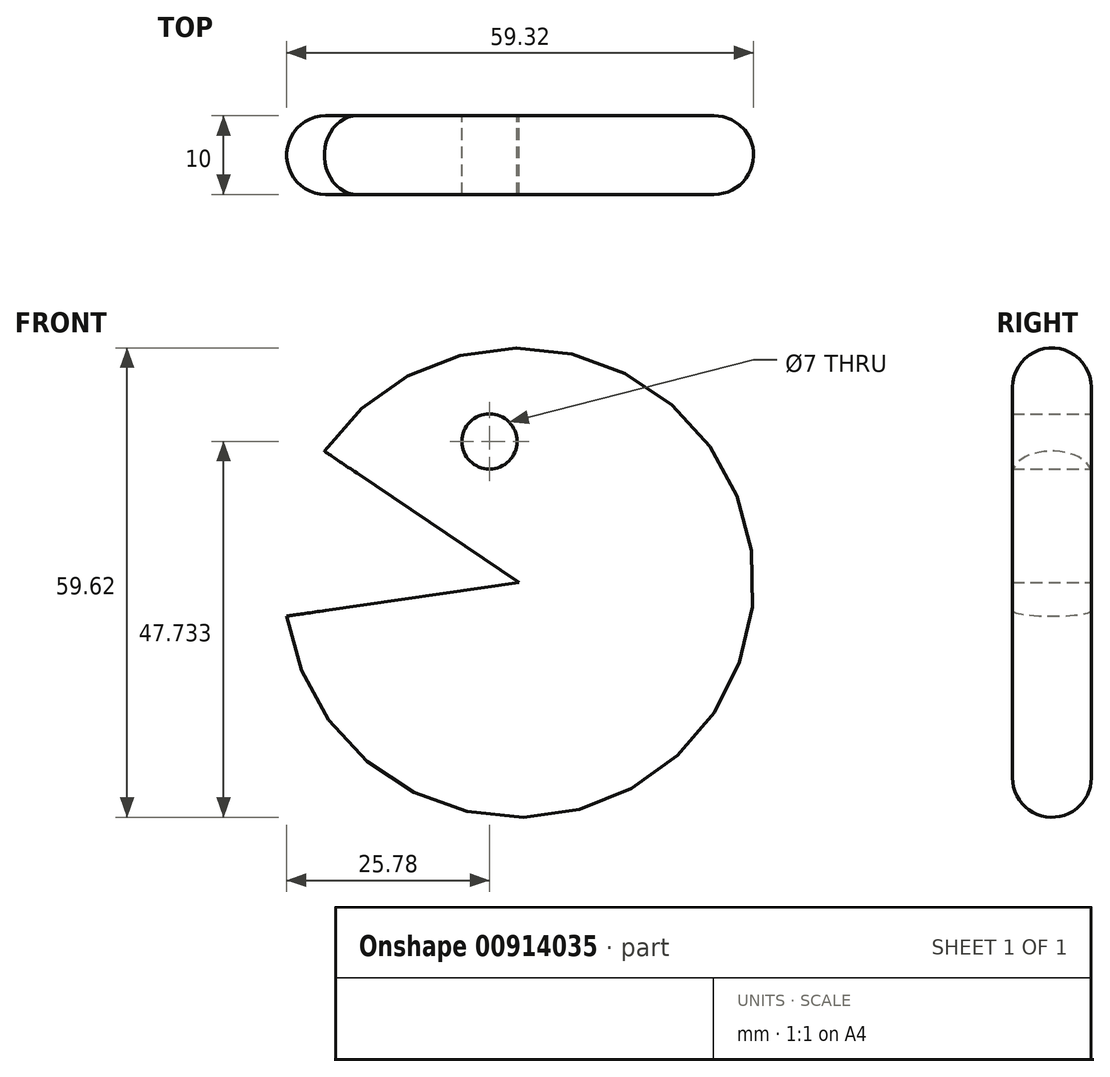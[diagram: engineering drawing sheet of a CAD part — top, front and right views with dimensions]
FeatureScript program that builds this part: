
annotation { "Feature Type Name" : "Feature", "Feature Type Description" : "" }
export const myFeature = defineFeature(function(context is Context, id is Id, definition is map)
    precondition{}
    {
        {
            var Q0;
            Q0=qCreatedBy(makeId("Front.planeOp"),FACE);
            var sketch = newSketch(context, id + "F0", { "sketchPlane" : qUnion([Q0])});
            skArc(sketch, "E0", {"start": v(-29.5, -4.27) * mm, "mid": v(29.06, -6.66) * mm, "end": v(-24.7, 16.7) * mm});
            skLineSegment(sketch, "E1", {"start": v(-24.7, 16.7) * mm, "end": v(0, 0) * mm});
            skLineSegment(sketch, "E2", {"start": v(0, 0) * mm, "end": v(-29.5, -4.27) * mm});
            skCircle(sketch, "E3", {"center": v(-3.73, 17.92) * mm, "radius": 3.5 * mm});
            skSolve(sketch);
        }
        {
            var Q0;
            Q0 = qSketchRegion(id + "F0", true);
            extrude(context, id + "F1", {"entities" : qUnion([Q0]), "depth" : 10 * mm, "offsetDistance" : 25 * mm});
        }
        {
            var Q0;
            Q0=makeQuery(id+"F1.opExtrude","CAP_EDGE",EDGE,{"disambiguationData":[OSD([sQuery(id+"F0.wireOp",EDGE,"E0")])],"isStart":false});
            var Q1;
            Q1=makeQuery(id+"F1.opExtrude","CAP_EDGE",EDGE,{"disambiguationData":[OSD([sQuery(id+"F0.wireOp",EDGE,"E0")])],"isStart":true});
            fillet(context, id + "F2", {"entities" : qUnion([Q0, Q1]), "radius" : 5 * mm, "tangentPropagation" : true, "allowEdgeOverflow" : false});
        }
    });
